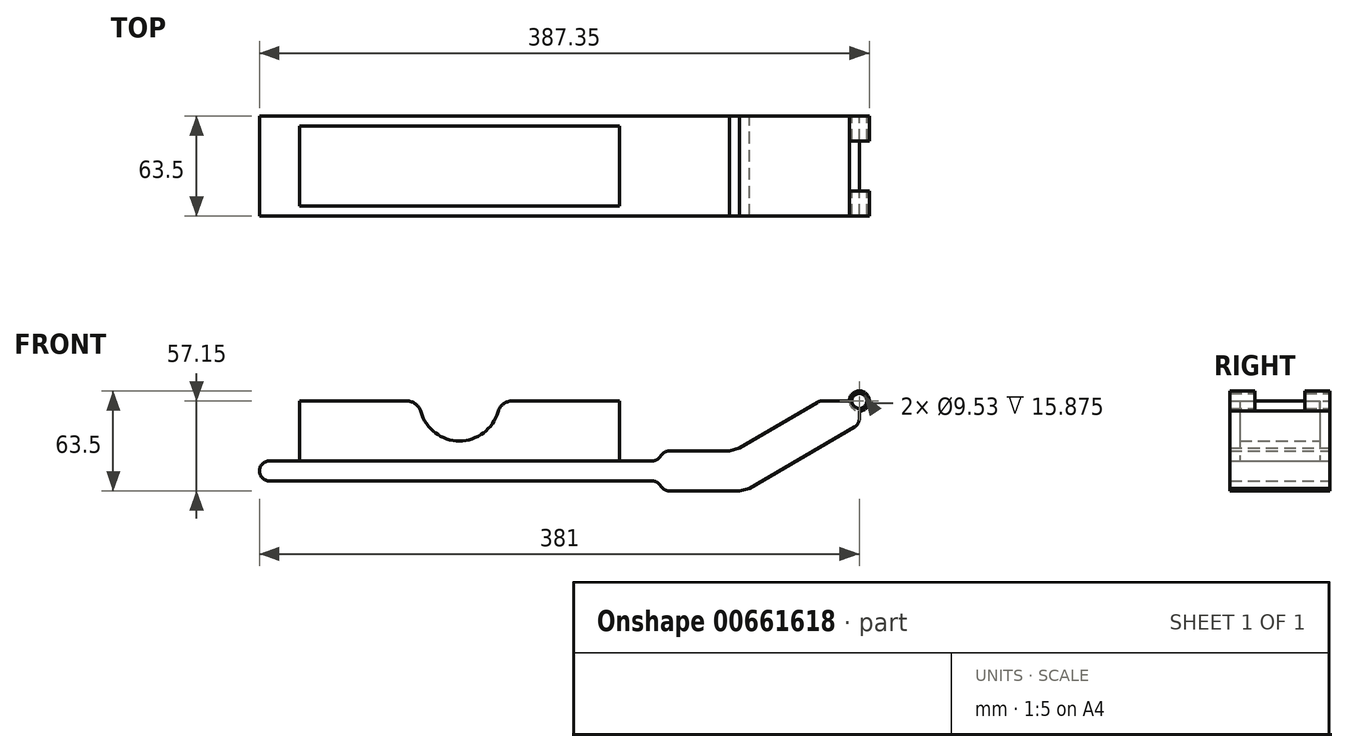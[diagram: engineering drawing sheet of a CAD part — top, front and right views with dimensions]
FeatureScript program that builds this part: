
annotation { "Feature Type Name" : "Feature", "Feature Type Description" : "" }
export const myFeature = defineFeature(function(context is Context, id is Id, definition is map)
    precondition{}
    {
        {
            var Q0;
            Q0=qCreatedBy(makeId("Front.planeOp"),FACE);
            var sketch = newSketch(context, id + "F0", { "sketchPlane" : qUnion([Q0])});
            skLineSegment(sketch, "E0", {"start": v(0, 0) * mm, "end": v(-4.76, 0) * mm});
            skCircle(sketch, "E1", {"center": v(0, 0) * mm, "radius": 4.76 * mm});
            skArc(sketch, "E2", {"start": v(0, -6.35) * mm, "mid": v(4.5, 4.5) * mm, "end": v(-6.35, 0) * mm});
            skLineSegment(sketch, "E3", {"start": v(-355.6, 0) * mm, "end": v(-355.6, -38.1) * mm});
            skLineSegment(sketch, "E4", {"start": v(-152.4, 0) * mm, "end": v(-152.4, -38.1) * mm});
            skLineSegment(sketch, "E5", {"start": v(-152.4, -38.1) * mm, "end": v(-355.6, -38.1) * mm});
            skLineSegment(sketch, "E6", {"start": v(-355.6, -38.1) * mm, "end": v(-374.65, -38.1) * mm});
            skLineSegment(sketch, "E7", {"start": v(-381, -44.45) * mm, "end": v(-381, -44.45) * mm});
            skLineSegment(sketch, "E8", {"start": v(-374.65, -50.8) * mm, "end": v(-131.65, -50.8) * mm});
            skLineSegment(sketch, "E9", {"start": v(-131.65, -38.1) * mm, "end": v(-152.4, -38.1) * mm});
            skLineSegment(sketch, "E10", {"start": v(0, -6.35) * mm, "end": v(0, -11.06) * mm});
            skPoint(sketch, "E10.endSnap0", {"position": v(-127, -44.45) * mm});
            skLineSegment(sketch, "E11.0", {"start": v(-76.2, -57.15) * mm, "end": v(-120.65, -57.15) * mm});
            skLineSegment(sketch, "E12.0", {"start": v(-82.6, -31.75) * mm, "end": v(-120.65, -31.75) * mm});
            skLineSegment(sketch, "E13.0", {"start": v(-76.2, -29.75) * mm, "end": v(-26.69, -0.87) * mm});
            skLineSegment(sketch, "E14.0", {"start": v(-69.8, -55.42) * mm, "end": v(-3.15, -16.54) * mm});
            skLineSegment(sketch, "E15", {"start": v(-127, -38.1) * mm, "end": v(-127, -38.1) * mm});
            skLineSegment(sketch, "E16", {"start": v(-127, -50.8) * mm, "end": v(-127, -50.8) * mm});
            skLineSegment(sketch, "E17", {"start": v(-76.2, -57.15) * mm, "end": v(-69.8, -55.42) * mm});
            skLineSegment(sketch, "E18", {"start": v(-82.6, -31.75) * mm, "end": v(-76.2, -29.75) * mm});
            skPoint(sketch, "E19.orphan", {"position": v(-82.6, -33.48) * mm});
            skPoint(sketch, "E20.orphan", {"position": v(-76.2, -31.75) * mm});
            skPoint(sketch, "E21.orphan", {"position": v(0, -44.45) * mm});
            skPoint(sketch, "E22.visualSharp", {"position": v(-127, -31.75) * mm});
            skArc(sketch, "E22.filletArc", {"start": v(-120.65, -31.75) * mm, "mid": v(-123.83, -32.6) * mm, "end": v(-126.15, -34.92) * mm});
            skPoint(sketch, "E23.visualSharp", {"position": v(-127, -57.15) * mm});
            skArc(sketch, "E23.filletArc", {"start": v(-126.15, -53.98) * mm, "mid": v(-123.82, -56.3) * mm, "end": v(-120.65, -57.15) * mm});
            skPoint(sketch, "E24.visualSharp", {"position": v(-127, -38.1) * mm});
            skArc(sketch, "E24.filletArc", {"start": v(-131.65, -38.1) * mm, "mid": v(-128.47, -37.25) * mm, "end": v(-126.15, -34.93) * mm});
            skPoint(sketch, "E25.visualSharp", {"position": v(-127, -50.8) * mm});
            skArc(sketch, "E25.filletArc", {"start": v(-126.15, -53.98) * mm, "mid": v(-128.47, -51.65) * mm, "end": v(-131.65, -50.8) * mm});
            skPoint(sketch, "E26.visualSharp", {"position": v(-381, -50.8) * mm});
            skArc(sketch, "E26.filletArc", {"start": v(-381, -44.45) * mm, "mid": v(-379.14, -48.94) * mm, "end": v(-374.65, -50.8) * mm});
            skPoint(sketch, "E27.visualSharp", {"position": v(-381, -38.1) * mm});
            skArc(sketch, "E27.filletArc", {"start": v(-374.65, -38.1) * mm, "mid": v(-379.14, -39.96) * mm, "end": v(-381, -44.45) * mm});
            skPoint(sketch, "E28.visualSharp", {"position": v(0, -14.7) * mm});
            skArc(sketch, "E28.filletArc", {"start": v(-3.15, -16.54) * mm, "mid": v(-0.84, -14.22) * mm, "end": v(0, -11.06) * mm});
            skPoint(sketch, "E29.visualSharp", {"position": v(-25.2, 0) * mm});
            skArc(sketch, "E29.filletArc", {"start": v(-23.49, 0) * mm, "mid": v(-25.15, -0.22) * mm, "end": v(-26.69, -0.87) * mm});
            skLineSegment(sketch, "E30.trimOffspring", {"start": v(-6.35, 0) * mm, "end": v(-23.49, 0) * mm});
            skLineSegment(sketch, "E31.trimOffspring", {"start": v(-6.35, 0) * mm, "end": v(-25.2, 0) * mm});
            skLineSegment(sketch, "E32.trimOffspring", {"start": v(-152.4, 0) * mm, "end": v(-220.4, 0) * mm});
            skPoint(sketch, "E33.start.orphan", {"position": v(-381, 0) * mm});
            skArc(sketch, "E34", {"start": v(-278.44, -6.93) * mm, "mid": v(-254, -25.4) * mm, "end": v(-229.56, -6.93) * mm});
            skLineSegment(sketch, "E35.trimOffspring", {"start": v(-287.6, 0) * mm, "end": v(-355.6, 0) * mm});
            skPoint(sketch, "E36.visualSharp", {"position": v(-279.4, 0) * mm});
            skArc(sketch, "E36.filletArc", {"start": v(-278.44, -6.93) * mm, "mid": v(-281.86, -1.93) * mm, "end": v(-287.6, 0) * mm});
            skPoint(sketch, "E37.visualSharp", {"position": v(-228.6, 0) * mm});
            skArc(sketch, "E37.filletArc", {"start": v(-220.4, 0) * mm, "mid": v(-226.14, -1.93) * mm, "end": v(-229.56, -6.93) * mm});
            skSolve(sketch);
        }
        {
            var Q0;
            Q0=makeQuery(id+"F0.imprint","IMPRINT",FACE,{"disambiguationData":[TD([[makeQuery(id+"F0.imprint","IMPRINT",EDGE,{"derivedFrom":sQuery(id+"F0.wireOp",EDGE,"E1")}),-1.0]])]});
            extrude(context, id + "F1", {"entities" : qUnion([Q0]), "depth" : 31.75 * mm, "offsetDistance" : 25.4 * mm, "hasSecondDirection" : true, "secondDirectionOppositeDirection" : true, "secondDirectionDepth" : 31.75 * mm});
        }
        {
            var Q0;
            Q0 = qSketchRegion(id + "F0", true);
            extrude(context, id + "F2", {"entities" : qUnion([Q0]), "operationType" : NewBodyOperationType.ADD, "depth" : 25.4 * mm, "offsetDistance" : 25.4 * mm, "hasSecondDirection" : true, "secondDirectionOppositeDirection" : true, "secondDirectionDepth" : 25.4 * mm});
        }
        {
            var Q0;
            Q0=makeQuery(id+"F1.opExtrude","CAP_FACE",FACE,{"disambiguationData":[OSD([sQuery(id+"F0.wireOp",EDGE,"E1"),sQuery(id+"F0.wireOp",EDGE,"E2"),sQuery(id+"F0.wireOp",EDGE,"E5"),sQuery(id+"F0.wireOp",EDGE,"E6"),sQuery(id+"F0.wireOp",EDGE,"E8"),sQuery(id+"F0.wireOp",EDGE,"E9"),sQuery(id+"F0.wireOp",EDGE,"E10"),sQuery(id+"F0.wireOp",EDGE,"E11.0"),sQuery(id+"F0.wireOp",EDGE,"E12.0"),sQuery(id+"F0.wireOp",EDGE,"E13.0"),sQuery(id+"F0.wireOp",EDGE,"E14.0"),sQuery(id+"F0.wireOp",EDGE,"E17"),sQuery(id+"F0.wireOp",EDGE,"E18"),sQuery(id+"F0.wireOp",EDGE,"E22.filletArc"),sQuery(id+"F0.wireOp",EDGE,"E23.filletArc"),sQuery(id+"F0.wireOp",EDGE,"E24.filletArc"),sQuery(id+"F0.wireOp",EDGE,"E25.filletArc"),sQuery(id+"F0.wireOp",EDGE,"E26.filletArc"),sQuery(id+"F0.wireOp",EDGE,"E27.filletArc"),sQuery(id+"F0.wireOp",EDGE,"E28.filletArc"),sQuery(id+"F0.wireOp",EDGE,"E29.filletArc"),sQuery(id+"F0.wireOp",EDGE,"E31.trimOffspring")])],"isStart":false});
            cPlane(context, id + "F3", {"entities" : qUnion([Q0]), "cplaneType" : CPlaneType.OFFSET, "offset" : 15.88 * mm, "oppositeDirection" : true, "width" : 152.4 * mm, "height" : 152.4 * mm});
        }
        {
            var Q0;
            Q0=qCreatedBy(id+"F3.planeOp",FACE);
            var sketch = newSketch(context, id + "F4", { "sketchPlane" : qUnion([Q0])});
            skCircle(sketch, "E38", {"center": v(0, 0) * mm, "radius": 6.35 * mm});
            skSolve(sketch);
        }
        {
            var Q0;
            Q0 = qSketchRegion(id + "F4", true);
            extrude(context, id + "F5", {"entities" : qUnion([Q0]), "operationType" : NewBodyOperationType.REMOVE, "oppositeDirection" : true, "depth" : 31.75 * mm, "offsetDistance" : 25.4 * mm});
        }
    });
